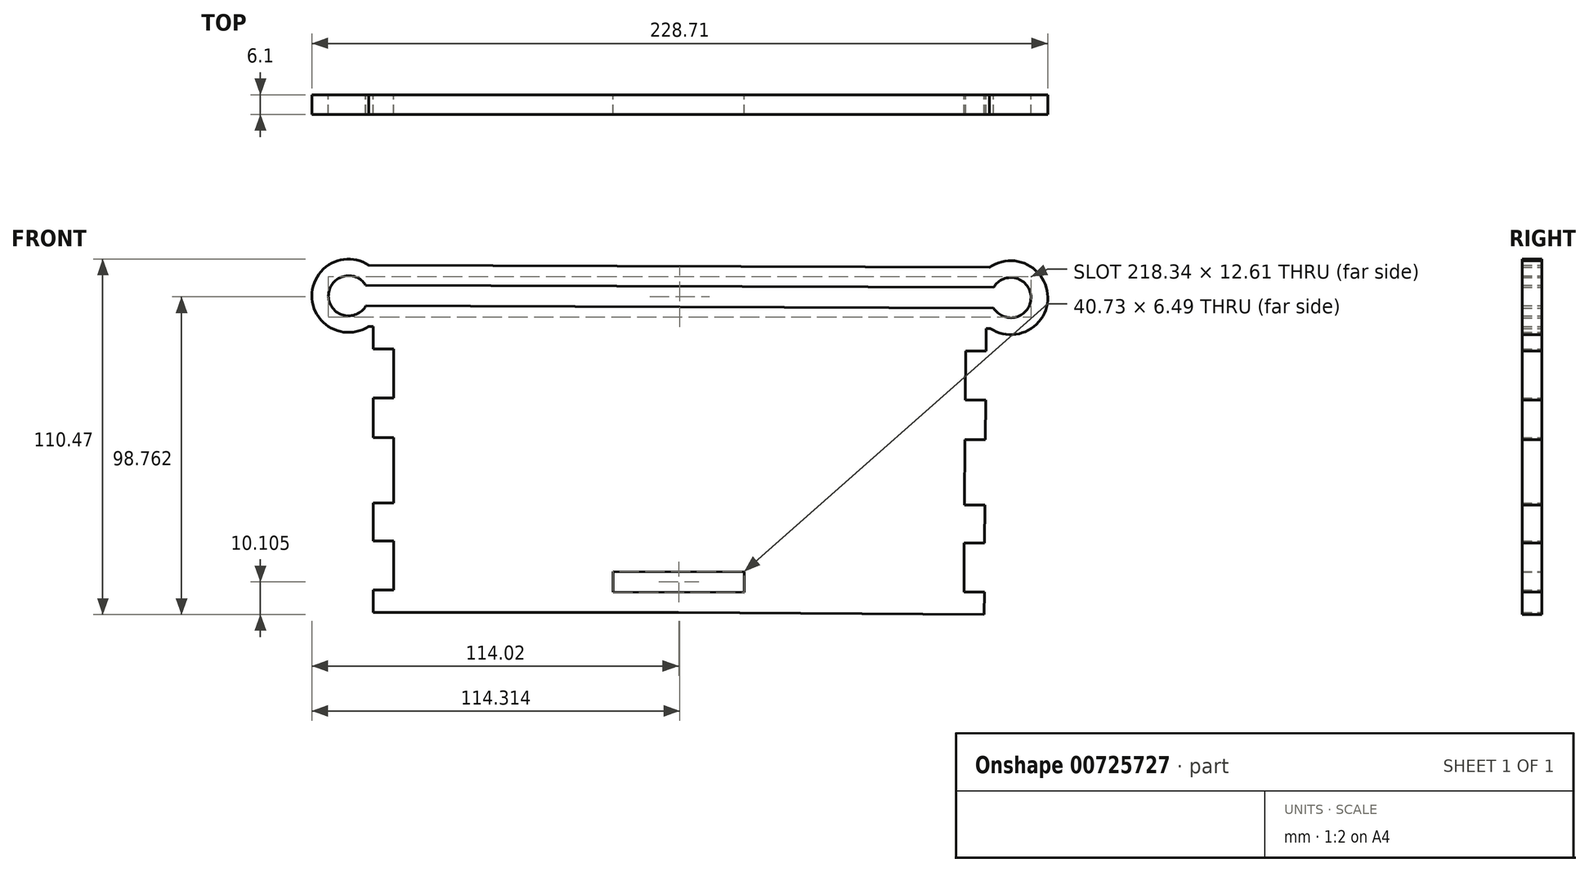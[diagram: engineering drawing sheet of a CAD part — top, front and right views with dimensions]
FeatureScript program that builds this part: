
annotation { "Feature Type Name" : "Feature", "Feature Type Description" : "" }
export const myFeature = defineFeature(function(context is Context, id is Id, definition is map)
    precondition{}
    {
        {
            var Q0;
            Q0=qCreatedBy(makeId("Front.planeOp"),FACE);
            var sketch = newSketch(context, id + "F0", { "sketchPlane" : qUnion([Q0])});
            skLineSegment(sketch, "E0.bottom", {"start": v(0, 0) * mm, "end": v(94.97, 0) * mm});
            skLineSegment(sketch, "E1.right", {"start": v(74.65, 6.35) * mm, "end": v(74.65, 12.7) * mm});
            skPoint(sketch, "E2.trimOffspring.end.orphan", {"position": v(94.97, 0) * mm});
            skLineSegment(sketch, "E3.top", {"start": v(0, 54.3) * mm, "end": v(6.35, 54.3) * mm});
            skLineSegment(sketch, "E4.top", {"start": v(0, 33.98) * mm, "end": v(6.35, 33.98) * mm});
            skLineSegment(sketch, "E5", {"start": v(0, 0) * mm, "end": v(0, 6.98) * mm});
            skLineSegment(sketch, "E6", {"start": v(0, 88.9) * mm, "end": v(0, 81.91) * mm});
            skLineSegment(sketch, "E7", {"start": v(0, 54.3) * mm, "end": v(0, 66.67) * mm});
            skLineSegment(sketch, "E8.bottom", {"start": v(0, 22.22) * mm, "end": v(6.35, 22.22) * mm});
            skLineSegment(sketch, "E8.top", {"start": v(0, 6.98) * mm, "end": v(6.35, 6.98) * mm});
            skLineSegment(sketch, "E8.right", {"start": v(6.35, 22.22) * mm, "end": v(6.35, 6.98) * mm});
            skLineSegment(sketch, "E9.bottom", {"start": v(0, 66.67) * mm, "end": v(6.35, 66.67) * mm});
            skLineSegment(sketch, "E9.top", {"start": v(0, 81.91) * mm, "end": v(6.35, 81.91) * mm});
            skLineSegment(sketch, "E9.right", {"start": v(6.35, 66.67) * mm, "end": v(6.35, 81.91) * mm});
            skLineSegment(sketch, "E10.trimOffspring", {"start": v(0, 66.67) * mm, "end": v(0, 54.3) * mm});
            skLineSegment(sketch, "E11.trimOffspring", {"start": v(0, 81.91) * mm, "end": v(0, 88.9) * mm});
            skLineSegment(sketch, "E12.trimOffspring", {"start": v(0, 6.98) * mm, "end": v(0, 0) * mm});
            skLineSegment(sketch, "E13.trimOffspring", {"start": v(0, 22.22) * mm, "end": v(0, 33.98) * mm});
            skPoint(sketch, "E14.orphan", {"position": v(0, 22.22) * mm});
            skLineSegment(sketch, "E15.MirrorCS", {"start": v(190.3, 53.64) * mm, "end": v(190.39, 66.02) * mm});
            skLineSegment(sketch, "E16.MirrorCS", {"start": v(189.93, -0.65) * mm, "end": v(189.98, 6.34) * mm});
            skLineSegment(sketch, "E17.MirrorCS", {"start": v(190.54, 88.25) * mm, "end": v(190.5, 81.26) * mm});
            skLineSegment(sketch, "E18.MirrorCS", {"start": v(190.39, 66.02) * mm, "end": v(190.3, 53.64) * mm});
            skLineSegment(sketch, "E19.MirrorCS", {"start": v(190.08, 21.57) * mm, "end": v(183.73, 21.62) * mm});
            skLineSegment(sketch, "E20.MirrorCS", {"start": v(189.98, 6.34) * mm, "end": v(189.93, -0.65) * mm});
            skLineSegment(sketch, "E21.MirrorCS", {"start": v(183.73, 21.62) * mm, "end": v(183.63, 6.38) * mm});
            skLineSegment(sketch, "E22.MirrorCS", {"start": v(115.33, 6.21) * mm, "end": v(115.37, 12.56) * mm});
            skLineSegment(sketch, "E23.MirrorCS", {"start": v(190.5, 81.26) * mm, "end": v(184.14, 81.3) * mm});
            skPoint(sketch, "E24.MirrorP", {"position": v(190.08, 21.57) * mm});
            skLineSegment(sketch, "E25.MirrorCS", {"start": v(189.93, -0.65) * mm, "end": v(94.97, 0) * mm});
            skLineSegment(sketch, "E26.MirrorCS", {"start": v(189.98, 6.34) * mm, "end": v(183.63, 6.38) * mm});
            skLineSegment(sketch, "E27.MirrorCS", {"start": v(190.5, 81.26) * mm, "end": v(190.54, 88.25) * mm});
            skLineSegment(sketch, "E28.MirrorCS", {"start": v(190.3, 53.64) * mm, "end": v(183.95, 53.69) * mm});
            skLineSegment(sketch, "E29.MirrorCS", {"start": v(190.39, 66.02) * mm, "end": v(184.04, 66.07) * mm});
            skLineSegment(sketch, "E30.MirrorCS", {"start": v(184.04, 66.07) * mm, "end": v(184.14, 81.3) * mm});
            skLineSegment(sketch, "E31.MirrorCS", {"start": v(190.08, 21.57) * mm, "end": v(190.16, 33.33) * mm});
            skLineSegment(sketch, "E32.MirrorCS", {"start": v(190.16, 33.33) * mm, "end": v(183.81, 33.37) * mm});
            skLineSegment(sketch, "E33", {"start": v(-1.3, 107.9) * mm, "end": v(191.6, 107.25) * mm});
            skLineSegment(sketch, "E34", {"start": v(-1.37, 88.9) * mm, "end": v(0, 88.9) * mm});
            skLineSegment(sketch, "E35", {"start": v(183.95, 53.69) * mm, "end": v(183.81, 33.37) * mm});
            skLineSegment(sketch, "E36", {"start": v(191.87, 88.24) * mm, "end": v(190.54, 88.25) * mm});
            skLineSegment(sketch, "E37", {"start": v(6.35, 54.3) * mm, "end": v(6.35, 33.98) * mm});
            skLineSegment(sketch, "E38", {"start": v(-2.32, 101.73) * mm, "end": v(192.88, 101.07) * mm});
            skLineSegment(sketch, "E39", {"start": v(192.86, 94.64) * mm, "end": v(-2.2, 95.3) * mm});
            skLineSegment(sketch, "E40", {"start": v(74.65, 12.7) * mm, "end": v(115.37, 12.56) * mm});
            skLineSegment(sketch, "E41", {"start": v(115.33, 6.21) * mm, "end": v(74.65, 6.35) * mm});
            skArc(sketch, "E42", {"start": v(-1.3, 107.9) * mm, "mid": v(-19.01, 98.46) * mm, "end": v(-1.37, 88.9) * mm});
            skPoint(sketch, "E42.centerSnap0", {"position": v(-13.87, 98.42) * mm});
            skPoint(sketch, "E43.orphan", {"position": v(-13.87, 107.95) * mm});
            skPoint(sketch, "E44.start.orphan", {"position": v(-13.87, 88.9) * mm});
            skArc(sketch, "E45", {"start": v(-2.32, 101.73) * mm, "mid": v(-13.87, 98.31) * mm, "end": v(-2.2, 95.3) * mm});
            skArc(sketch, "E46", {"start": v(191.87, 88.24) * mm, "mid": v(209.7, 98) * mm, "end": v(191.6, 107.25) * mm});
            skArc(sketch, "E47", {"start": v(192.86, 94.64) * mm, "mid": v(204.47, 97.81) * mm, "end": v(192.88, 101.07) * mm});
            skSolve(sketch);
        }
        {
            var Q0;
            Q0=makeQuery(id+"F0.imprint","IMPRINT",FACE,{"disambiguationData":[TD([[makeQuery(id+"F0.imprint","IMPRINT",EDGE,{"derivedFrom":sQuery(id+"F0.wireOp",EDGE,"E0.bottom")}),1.0]])]});
            extrude(context, id + "F1", {"entities" : qUnion([Q0]), "depth" : 6.1 * mm, "offsetDistance" : 25.4 * mm});
        }
    });
